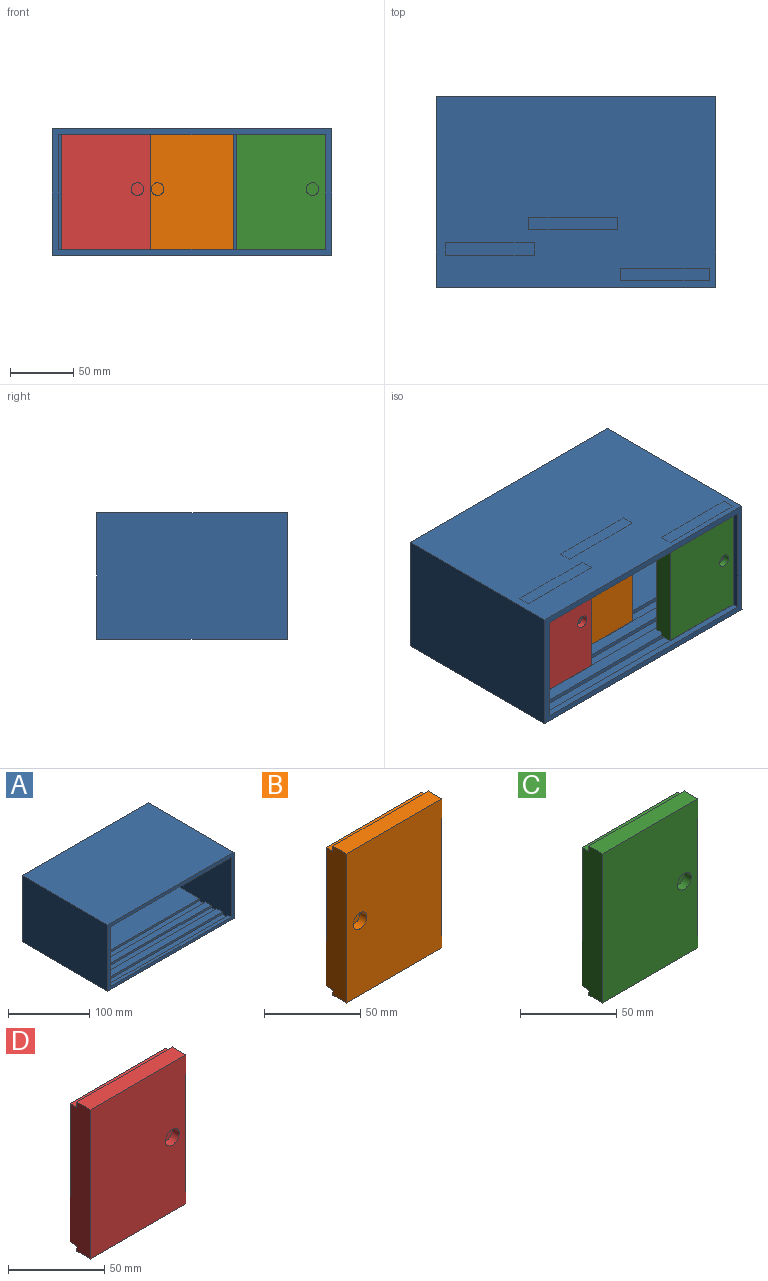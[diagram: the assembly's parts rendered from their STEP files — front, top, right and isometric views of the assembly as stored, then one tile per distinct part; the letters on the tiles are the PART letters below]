
ASSEMBLY  parts=4 mates=3
PART A: 35 faces, bbox 220x150x100 mm
  f0: plane 210x10mm, normal (0,0,-1), area 2100mm2, adj f13,f14,f29,f32
  f1: plane 210x10mm, normal (0,0,-1), area 2100mm2, adj f13,f14,f26,f30
  f2: plane 210x90mm, normal (0,0,-1), area 18900mm2, adj f12,f13,f14,f27
  f3: plane 210x10mm, normal (0,0,1), area 2100mm2, adj f13,f14,f21,f25
  f4: plane 210x10mm, normal (0,0,1), area 2100mm2, adj f13,f14,f18,f22
  f5: plane 210x90mm, normal (0,0,1), area 18900mm2, adj f12,f13,f14,f19
  f6: plane 220x100mm, normal (0,-1,0), area 3100mm2, adj f8,f9,f10,f11,f13,f14,f15,f16
  f7: plane 220x100mm, normal (0,1,0), area 22000mm2, adj f8,f9,f10,f11
  f8: plane 150x100mm, normal (-1,0,0), area 15000mm2, adj f6,f7,f10,f11
  f9: plane 150x100mm, normal (1,0,0), area 15000mm2, adj f6,f7,f10,f11
  f10: plane 220x150mm, normal (0,0,1), area 33000mm2, adj f6,f7,f8,f9
  f11: plane 220x150mm, normal (0,0,-1), area 33000mm2, adj f6,f7,f8,f9
  f12: plane 210x90mm, normal (0,-1,0), area 18900mm2, adj f2,f5,f13,f14
  f13: plane 145x96.6mm, normal (1,0,0), area 13248mm2, adj f0,f1,f2,f3,f4,f5,f6,f12
  f14: plane 145x96.6mm, normal (-1,0,0), area 13248mm2, adj f0,f1,f2,f3,f4,f5,f6,f12
  f15: plane 210x5mm, normal (0,0,-1), area 1050mm2, adj f6,f13,f14,f33
  f16: plane 210x5mm, normal (0,0,1), area 1050mm2, adj f6,f13,f14,f24
  f17: plane 210x10mm, normal (0,0,1), area 2100mm2, adj f13,f14,f18,f19
  f18: plane 210x3.3mm, normal (0,1,0), area 693mm2, adj f4,f13,f14,f17
  f19: plane 210x3.3mm, normal (0,-1,0), area 693mm2, adj f5,f13,f14,f17
  f20: plane 210x10mm, normal (0,0,1), area 2100mm2, adj f13,f14,f21,f22
  f21: plane 210x3.3mm, normal (0,1,0), area 693mm2, adj f3,f13,f14,f20
  f22: plane 210x3.3mm, normal (0,-1,0), area 693mm2, adj f4,f13,f14,f20
  f23: plane 210x10mm, normal (0,0,1), area 2100mm2, adj f13,f14,f24,f25
  f24: plane 210x3.3mm, normal (0,1,0), area 693mm2, adj f13,f14,f16,f23
  f25: plane 210x3.3mm, normal (0,-1,0), area 693mm2, adj f3,f13,f14,f23
  f26: plane 210x3.3mm, normal (0,1,0), area 693mm2, adj f1,f13,f14,f28
  f27: plane 210x3.3mm, normal (0,-1,0), area 693mm2, adj f2,f13,f14,f28
  f28: plane 210x10mm, normal (0,0,-1), area 2100mm2, adj f13,f14,f26,f27
  f29: plane 210x3.3mm, normal (0,1,0), area 693mm2, adj f0,f13,f14,f31
  f30: plane 210x3.3mm, normal (0,-1,0), area 693mm2, adj f1,f13,f14,f31
  f31: plane 210x10mm, normal (0,0,-1), area 2100mm2, adj f13,f14,f29,f30
  f32: plane 210x3.3mm, normal (0,-1,0), area 693mm2, adj f0,f13,f14,f34
  f33: plane 210x3.3mm, normal (0,1,0), area 693mm2, adj f13,f14,f15,f34
  f34: plane 210x10mm, normal (0,0,-1), area 2100mm2, adj f13,f14,f32,f33
PART B: 12 faces, bbox 70x15x94.6 mm
  f0: plane 94.6x70mm, normal (0,-1,0), area 6543.5mm2, adj f3,f4,f5,f8,f10
  f1: plane 88x70mm, normal (0,1,0), area 6160mm2, adj f3,f4,f7,f9
  f2: plane 70x3.3mm, normal (0,1,0), area 231mm2, adj f3,f4,f8,f9
  f3: plane 94.6x15mm, normal (1,0,0), area 1386mm2, adj f0,f1,f2,f5,f6,f7,f8,f9
  f4: plane 94.6x15mm, normal (-1,0,0), area 1386mm2, adj f0,f1,f2,f5,f6,f7,f8,f9
  f5: plane 70x10mm, normal (0,0,-1), area 700mm2, adj f0,f3,f4,f6
  f6: plane 70x3.3mm, normal (0,1,0), area 231mm2, adj f3,f4,f5,f7
  f7: plane 70x5mm, normal (0,0,-1), area 350mm2, adj f1,f3,f4,f6
  f8: plane 70x10mm, normal (0,0,1), area 700mm2, adj f0,f2,f3,f4
  f9: plane 70x5mm, normal (0,0,1), area 350mm2, adj f1,f2,f3,f4
  f10: cylinder r=5mm len=10mm, axis (0,-1,0), area 157.1mm2, adj f0,f11
  f11: plane 10x10mm, normal (0,-1,0), area 78.5mm2, adj f10
PART C: 12 faces, bbox 70x15x94.6 mm
  f0: plane 94.6x70mm, normal (0,-1,0), area 6543.5mm2, adj f3,f4,f5,f8,f10
  f1: plane 88x70mm, normal (0,1,0), area 6160mm2, adj f3,f4,f7,f9
  f2: plane 70x3.3mm, normal (0,1,0), area 231mm2, adj f3,f4,f8,f9
  f3: plane 94.6x15mm, normal (-1,0,0), area 1386mm2, adj f0,f1,f2,f5,f6,f7,f8,f9
  f4: plane 94.6x15mm, normal (1,0,0), area 1386mm2, adj f0,f1,f2,f5,f6,f7,f8,f9
  f5: plane 70x10mm, normal (0,0,-1), area 700mm2, adj f0,f3,f4,f6
  f6: plane 70x3.3mm, normal (0,1,0), area 231mm2, adj f3,f4,f5,f7
  f7: plane 70x5mm, normal (0,0,-1), area 350mm2, adj f1,f3,f4,f6
  f8: plane 70x10mm, normal (0,0,1), area 700mm2, adj f0,f2,f3,f4
  f9: plane 70x5mm, normal (0,0,1), area 350mm2, adj f1,f2,f3,f4
  f10: cylinder r=5mm len=10mm, axis (0,-1,0), area 157.1mm2, adj f0,f11
  f11: plane 10x10mm, normal (0,-1,0), area 78.5mm2, adj f10
PART D: 12 faces, bbox 70x15x94.6 mm
  f0: plane 94.6x70mm, normal (0,-1,0), area 6543.5mm2, adj f3,f4,f5,f8,f10
  f1: plane 88x70mm, normal (0,1,0), area 6160mm2, adj f3,f4,f7,f9
  f2: plane 70x3.3mm, normal (0,1,0), area 231mm2, adj f3,f4,f8,f9
  f3: plane 94.6x15mm, normal (-1,0,0), area 1386mm2, adj f0,f1,f2,f5,f6,f7,f8,f9
  f4: plane 94.6x15mm, normal (1,0,0), area 1386mm2, adj f0,f1,f2,f5,f6,f7,f8,f9
  f5: plane 70x10mm, normal (0,0,-1), area 700mm2, adj f0,f3,f4,f6
  f6: plane 70x3.3mm, normal (0,1,0), area 231mm2, adj f3,f4,f5,f7
  f7: plane 70x5mm, normal (0,0,-1), area 350mm2, adj f1,f3,f4,f6
  f8: plane 70x10mm, normal (0,0,1), area 700mm2, adj f0,f2,f3,f4
  f9: plane 70x5mm, normal (0,0,1), area 350mm2, adj f1,f2,f3,f4
  f10: cylinder r=5mm len=10mm, axis (0,-1,0), area 157.1mm2, adj f0,f11
  f11: plane 10x10mm, normal (0,-1,0), area 78.5mm2, adj f10
PLACE A t=(-111.65,-8.79,-75.04)mm
PLACE B t=(-43.82,-8.79,-71.74)mm
PLACE C t=(-111.65,-8.79,-71.74)mm
PLACE D t=(-179.8,-8.79,-71.74)mm
MATE slider A.f13 <-> D.f3  axis (1,0,0) through (-216.65,-58.79,-70.04)mm
MATE slider A.f14 <-> C.f4  axis (-1,0,0) through (-6.65,-78.79,-70.04)mm
MATE slider A.f13 <-> B.f4  axis (1,0,0) through (-216.65,-38.79,-70.04)mm
